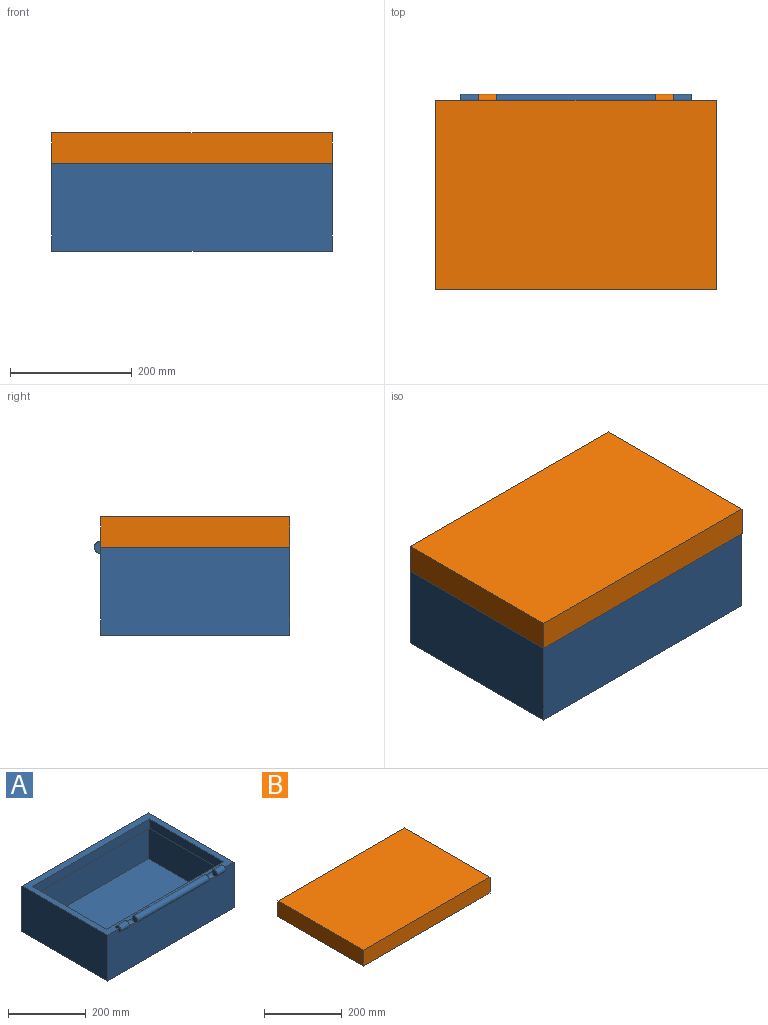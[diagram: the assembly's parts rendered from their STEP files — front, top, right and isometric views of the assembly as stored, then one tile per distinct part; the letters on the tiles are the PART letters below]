
ASSEMBLY  parts=2 mates=1
PART A: 27 faces, bbox 460x320x154 mm
  f0: cylinder r=10mm len=260mm, axis (-1,0,0), area 12252.2mm2, adj f4,f11,f24,f26
  f1: cylinder r=10mm len=30mm, axis (-1,0,0), area 471.2mm2, adj f4,f11,f20,f26
  f2: plane 460x144mm, normal (0,1,0), area 66240mm2, adj f3,f5,f6,f11
  f3: plane 310x144mm, normal (-1,0,0), area 44640mm2, adj f2,f4,f6,f11
  f4: plane 460x144mm, normal (0,-1,0), area 62440mm2, adj f0,f1,f3,f5,f6,f11,f18,f19
  f5: plane 310x144mm, normal (1,0,0), area 44640mm2, adj f2,f4,f6,f11
  f6: plane 460x310mm, normal (0,0,-1), area 142600mm2, adj f2,f3,f4,f5
  f7: plane 270x30mm, normal (1,0,0), area 8100mm2, adj f8,f10,f11,f12
  f8: plane 425x30mm, normal (0,-1,0), area 12750mm2, adj f7,f9,f11,f12
  f9: plane 270x30mm, normal (-1,0,0), area 8100mm2, adj f8,f10,f11,f12
  f10: plane 425x30mm, normal (0,1,0), area 12750mm2, adj f7,f9,f11,f12
  f11: plane 460x310mm, normal (0,0,1), area 24050mm2, adj f0,f1,f2,f3,f4,f5,f7,f8
  f12: plane 430x280mm, normal (0,0,-1), area 5650mm2, adj f7,f8,f9,f10,f14,f15,f16,f17
  f13: plane 430x280mm, normal (0,0,1), area 120400mm2, adj f14,f15,f16,f17
  f14: plane 430x99mm, normal (0,1,0), area 42570mm2, adj f12,f13,f15,f17
  f15: plane 280x99mm, normal (-1,0,0), area 27720mm2, adj f12,f13,f14,f16
  f16: plane 430x99mm, normal (0,-1,0), area 42570mm2, adj f12,f13,f15,f17
  f17: plane 280x99mm, normal (1,0,0), area 27720mm2, adj f12,f13,f14,f16
  f18: plane 20x20mm, normal (-1,0,0), area 235.6mm2, adj f4,f11,f19
  f19: cylinder r=10mm len=30mm, axis (-1,0,0), area 1413.7mm2, adj f4,f11,f18,f25
  f20: plane 20x20mm, normal (-1,0,0), area 314.2mm2, adj f1,f22
  f21: plane 20x20mm, normal (1,0,0), area 235.6mm2, adj f4,f11,f22
  f22: cylinder r=10mm len=30mm, axis (-1,0,0), area 1413.7mm2, adj f4,f11,f20,f21
  f23: cylinder r=10mm len=30mm, axis (-1,0,0), area 471.2mm2, adj f4,f11,f24,f25
  f24: plane 20x20mm, normal (-1,0,0), area 314.2mm2, adj f0,f23
  f25: plane 20x20mm, normal (1,0,0), area 314.2mm2, adj f19,f23
  f26: plane 20x20mm, normal (1,0,0), area 314.2mm2, adj f0,f1
PART B: 18 faces, bbox 460x320x60 mm
  f0: plane 460x50mm, normal (0,1,0), area 19800mm2, adj f1,f2,f4,f5,f12,f13,f14,f15
  f1: plane 460x310mm, normal (0,0,-1), area 24650mm2, adj f0,f2,f3,f4,f6,f7,f8,f9
  f2: plane 310x50mm, normal (-1,0,0), area 15500mm2, adj f0,f1,f3,f5
  f3: plane 460x50mm, normal (0,-1,0), area 23000mm2, adj f1,f2,f4,f5
  f4: plane 310x50mm, normal (1,0,0), area 15500mm2, adj f0,f1,f3,f5
  f5: plane 460x310mm, normal (0,0,1), area 142600mm2, adj f0,f2,f3,f4
  f6: plane 425x34mm, normal (0,-1,0), area 14450mm2, adj f1,f7,f9,f10
  f7: plane 270x34mm, normal (1,0,0), area 9180mm2, adj f1,f6,f8,f10
  f8: plane 425x34mm, normal (0,1,0), area 14450mm2, adj f1,f7,f9,f10
  f9: plane 270x34mm, normal (-1,0,0), area 9180mm2, adj f1,f6,f8,f10
  f10: plane 425x270mm, normal (0,0,-1), area 114750mm2, adj f6,f7,f8,f9
  f11: plane 20x20mm, normal (-1,0,0), area 314.2mm2, adj f12,f17
  f12: cylinder r=10mm len=30mm, axis (-1,0,0), area 1413.7mm2, adj f0,f1,f11,f13
  f13: plane 20x20mm, normal (1,0,0), area 235.6mm2, adj f0,f1,f12
  f14: plane 20x20mm, normal (-1,0,0), area 235.6mm2, adj f0,f1,f15
  f15: cylinder r=10mm len=30mm, axis (-1,0,0), area 1413.7mm2, adj f0,f1,f14,f16
  f16: plane 20x20mm, normal (1,0,0), area 314.2mm2, adj f15,f17
  f17: cylinder r=10mm len=260mm, axis (-1,0,0), area 4084.1mm2, adj f0,f1,f11,f16
PLACE A rot(axis=(0,0,1),180deg) t=(136.19,335.33,228.55)mm
PLACE B t=(136.19,335.33,372.55)mm
MATE revolute A.f0 <-> B.f12  axis (1,0,0) through (266.19,490.33,372.55)mm
